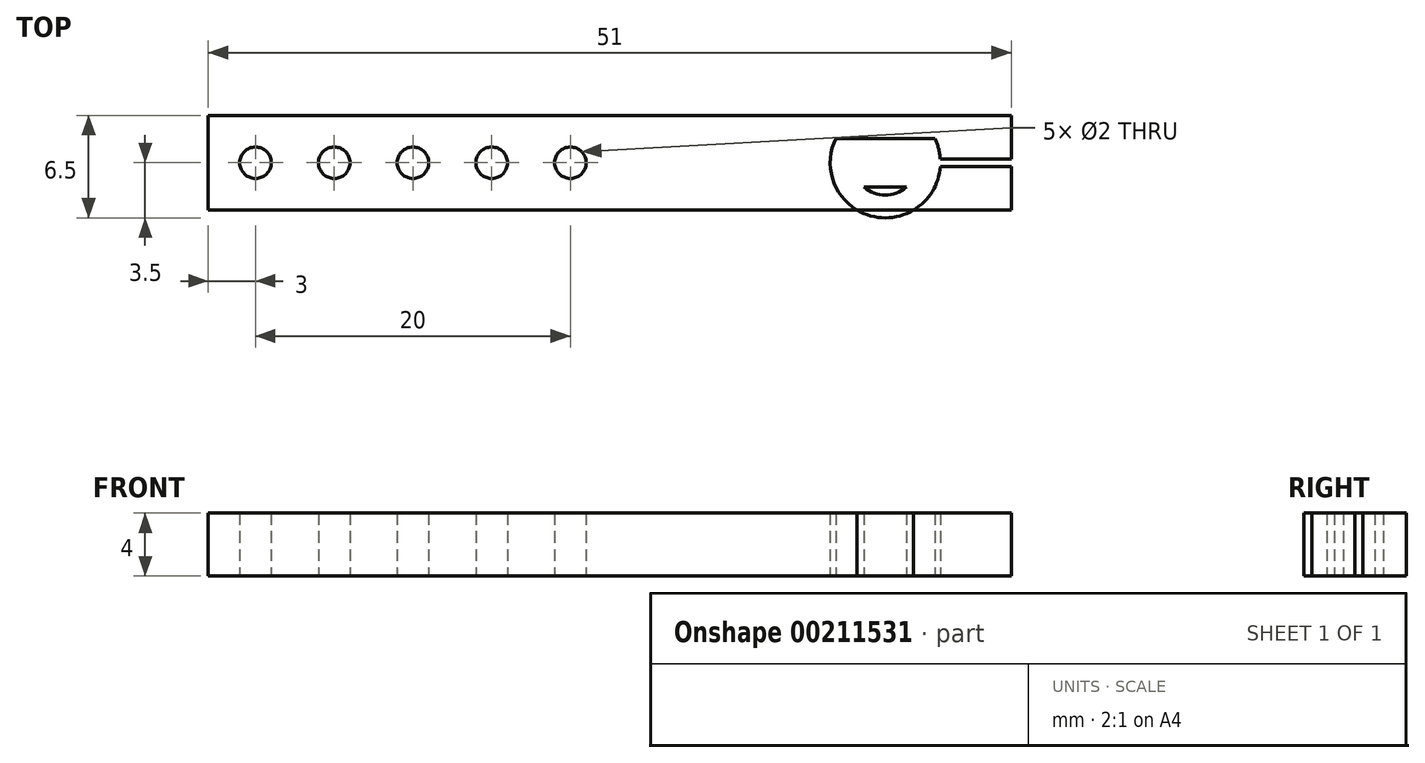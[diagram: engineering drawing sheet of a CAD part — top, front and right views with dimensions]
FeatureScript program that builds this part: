
annotation { "Feature Type Name" : "Feature", "Feature Type Description" : "" }
export const myFeature = defineFeature(function(context is Context, id is Id, definition is map)
    precondition{}
    {
        {
            var Q0;
            Q0=qCreatedBy(makeId("Top.planeOp"),FACE);
            var sketch = newSketch(context, id + "F0", { "sketchPlane" : qUnion([Q0])});
            skLineSegment(sketch, "E0.bottom", {"start": v(5.54, -1.55) * mm, "end": v(-5.54, -1.55) * mm});
            skLineSegment(sketch, "E0.top", {"start": v(5.54, 1.55) * mm, "end": v(-5.54, 1.55) * mm});
            skPoint(sketch, "E0.middle", {"position": v(0, 0) * mm});
            skCircle(sketch, "E1", {"center": v(0, 0) * mm, "radius": 3.5 * mm});
            skArc(sketch, "E2", {"start": v(1.34, -1.55) * mm, "mid": v(-1.55, -1.34) * mm, "end": v(-1.34, 1.55) * mm});
            skCircle(sketch, "E3", {"center": v(0, 0) * mm, "radius": 2.05 * mm});
            skLineSegment(sketch, "E4.bottom", {"start": v(8, 3) * mm, "end": v(-43, 3) * mm});
            skLineSegment(sketch, "E4.top", {"start": v(8, -3) * mm, "end": v(-43, -3) * mm});
            skLineSegment(sketch, "E4.left", {"start": v(8, 3) * mm, "end": v(8, -3) * mm});
            skLineSegment(sketch, "E4.right", {"start": v(-43, 3) * mm, "end": v(-43, -3) * mm});
            skPoint(sketch, "E4.middle", {"position": v(-17.5, 0) * mm});
            skCircle(sketch, "E5", {"center": v(-40, 0) * mm, "radius": 1 * mm});
            skCircle(sketch, "E6", {"center": v(-35, 0) * mm, "radius": 1 * mm});
            skCircle(sketch, "E7", {"center": v(-30, 0) * mm, "radius": 1 * mm});
            skCircle(sketch, "E8", {"center": v(-25, 0) * mm, "radius": 1 * mm});
            skCircle(sketch, "E9", {"center": v(-20, 0) * mm, "radius": 1 * mm});
            skPoint(sketch, "E10", {"position": v(-1.34, -1.55) * mm});
            skSolve(sketch);
        }
        {
            var Q0;
            {var subQ0=sQuery(id+"F0.wireOp",EDGE,"E4.right");Q0=makeQuery(id+"F0.imprint","IMPRINT",FACE,{"disambiguationData":[TD([[makeQuery(id+"F0.imprint","IMPRINT",EDGE,{"derivedFrom":subQ0}),1.0]])]});}
            var Q1;
            {var subQ0=sQuery(id+"F0.wireOp",EDGE,"E1");var subQ1=sQuery(id+"F0.wireOp",EDGE,"E0.bottom");var subQ2=makeQuery(id+"F0.imprint","INTERSECT",VERTEX,{"disambiguationData":[OD(1.0)],"derivedFrom":[subQ1,subQ0]});Q1=makeQuery(id+"F0.imprint","IMPRINT",FACE,{"disambiguationData":[TD([[makeQuery(id+"F0.imprint","IMPRINT",EDGE,{"disambiguationData":[TD([[subQ2,1.0]])],"derivedFrom":subQ1}),-1.0]])]});}
            var Q2;
            {var subQ0=sQuery(id+"F0.wireOp",EDGE,"E1");var subQ1=sQuery(id+"F0.wireOp",EDGE,"E0.bottom");var subQ2=makeQuery(id+"F0.imprint","INTERSECT",VERTEX,{"disambiguationData":[OD(0.0)],"derivedFrom":[subQ1,subQ0]});Q2=makeQuery(id+"F0.imprint","IMPRINT",FACE,{"disambiguationData":[TD([[makeQuery(id+"F0.imprint","IMPRINT",EDGE,{"disambiguationData":[TD([[subQ2,-1.0]])],"derivedFrom":subQ1}),1.0]])]});}
            var Q3;
            {var subQ0=sQuery(id+"F0.wireOp",EDGE,"E1");var subQ1=sQuery(id+"F0.wireOp",EDGE,"E0.top");var subQ5=makeQuery(id+"F0.imprint","INTERSECT",VERTEX,{"disambiguationData":[OD(0.0)],"derivedFrom":[subQ1,subQ0]});Q3=makeQuery(id+"F0.imprint","IMPRINT",FACE,{"disambiguationData":[TD([[makeQuery(id+"F0.imprint","IMPRINT",EDGE,{"disambiguationData":[TD([[subQ5,-1.0]])],"derivedFrom":subQ1}),-1.0]])]});}
            var Q4;
            {var subQ0=sQuery(id+"F0.wireOp",EDGE,"E3");var subQ1=sQuery(id+"F0.wireOp",EDGE,"E0.top");var subQ2=makeQuery(id+"F0.imprint","INTERSECT",VERTEX,{"disambiguationData":[OD(0.0)],"derivedFrom":[subQ1,subQ0]});Q4=makeQuery(id+"F0.imprint","IMPRINT",FACE,{"disambiguationData":[TD([[makeQuery(id+"F0.imprint","IMPRINT",EDGE,{"disambiguationData":[TD([[subQ2,-1.0]])],"derivedFrom":subQ1}),-1.0]])]});}
            var Q5;
            {var subQ0=sQuery(id+"F0.wireOp",EDGE,"E3");var subQ1=sQuery(id+"F0.wireOp",EDGE,"E0.bottom");var subQ2=makeQuery(id+"F0.imprint","INTERSECT",VERTEX,{"disambiguationData":[OD(0.0)],"derivedFrom":[subQ1,subQ0]});Q5=makeQuery(id+"F0.imprint","IMPRINT",FACE,{"disambiguationData":[TD([[makeQuery(id+"F0.imprint","IMPRINT",EDGE,{"disambiguationData":[TD([[subQ2,-1.0]])],"derivedFrom":subQ1}),1.0]])]});}
            var Q6;
            {var subQ0=sQuery(id+"F0.wireOp",EDGE,"E1");var subQ1=sQuery(id+"F0.wireOp",EDGE,"E0.bottom");var subQ2=makeQuery(id+"F0.imprint","INTERSECT",VERTEX,{"disambiguationData":[OD(0.0)],"derivedFrom":[subQ1,subQ0]});Q6=makeQuery(id+"F0.imprint","IMPRINT",FACE,{"disambiguationData":[TD([[makeQuery(id+"F0.imprint","IMPRINT",EDGE,{"disambiguationData":[TD([[subQ2,-1.0]])],"derivedFrom":subQ1}),-1.0]])]});}
            var Q7;
            {var subQ0=sQuery(id+"F0.wireOp",EDGE,"E4.left");Q7=makeQuery(id+"F0.imprint","IMPRINT",FACE,{"disambiguationData":[TD([[makeQuery(id+"F0.imprint","IMPRINT",EDGE,{"derivedFrom":subQ0}),-1.0]])]});}
            var Q8;
            {var subQ0=sQuery(id+"F0.wireOp",EDGE,"E4.top");var subQ1=sQuery(id+"F0.wireOp",EDGE,"E1");var subQ2=makeQuery(id+"F0.imprint","INTERSECT",VERTEX,{"disambiguationData":[OD(0.0)],"derivedFrom":[subQ1,subQ0]});Q8=makeQuery(id+"F0.imprint","IMPRINT",FACE,{"disambiguationData":[TD([[makeQuery(id+"F0.imprint","IMPRINT",EDGE,{"disambiguationData":[TD([[subQ2,-1.0]])],"derivedFrom":subQ1}),1.0]])]});}
            var Q9;
            {var subQ0=sQuery(id+"F0.wireOp",EDGE,"E4.bottom");var subQ1=sQuery(id+"F0.wireOp",EDGE,"E1");var subQ2=makeQuery(id+"F0.imprint","INTERSECT",VERTEX,{"disambiguationData":[OD(0.0)],"derivedFrom":[subQ1,subQ0]});Q9=makeQuery(id+"F0.imprint","IMPRINT",FACE,{"disambiguationData":[TD([[makeQuery(id+"F0.imprint","IMPRINT",EDGE,{"disambiguationData":[TD([[subQ2,-1.0]])],"derivedFrom":subQ1}),1.0]])]});}
            extrude(context, id + "F1", {"entities" : qUnion([Q0, Q1, Q2, Q3, Q4, Q5, Q6, Q7, Q8, Q9]), "endBound" : BoundingType.SYMMETRIC, "depth" : 4 * mm});
        }
        {
            var Q0;
            Q0=qCreatedBy(makeId("Right.planeOp"),FACE);
            var sketch = newSketch(context, id + "F2", { "sketchPlane" : qUnion([Q0])});
            skLineSegment(sketch, "E11.bottom", {"start": v(-0.25, -4.83) * mm, "end": v(0.25, -4.83) * mm});
            skLineSegment(sketch, "E11.top", {"start": v(-0.25, 4.83) * mm, "end": v(0.25, 4.83) * mm});
            skLineSegment(sketch, "E11.left", {"start": v(-0.25, -4.83) * mm, "end": v(-0.25, 4.83) * mm});
            skLineSegment(sketch, "E11.right", {"start": v(0.25, -4.83) * mm, "end": v(0.25, 4.83) * mm});
            skPoint(sketch, "E11.middle", {"position": v(0, 0) * mm});
            skSolve(sketch);
        }
        {
            var Q0;
            Q0 = qSketchRegion(id + "F2", true);
            extrude(context, id + "F3", {"entities" : qUnion([Q0]), "operationType" : NewBodyOperationType.REMOVE, "depth" : 25 * mm});
        }
    });
